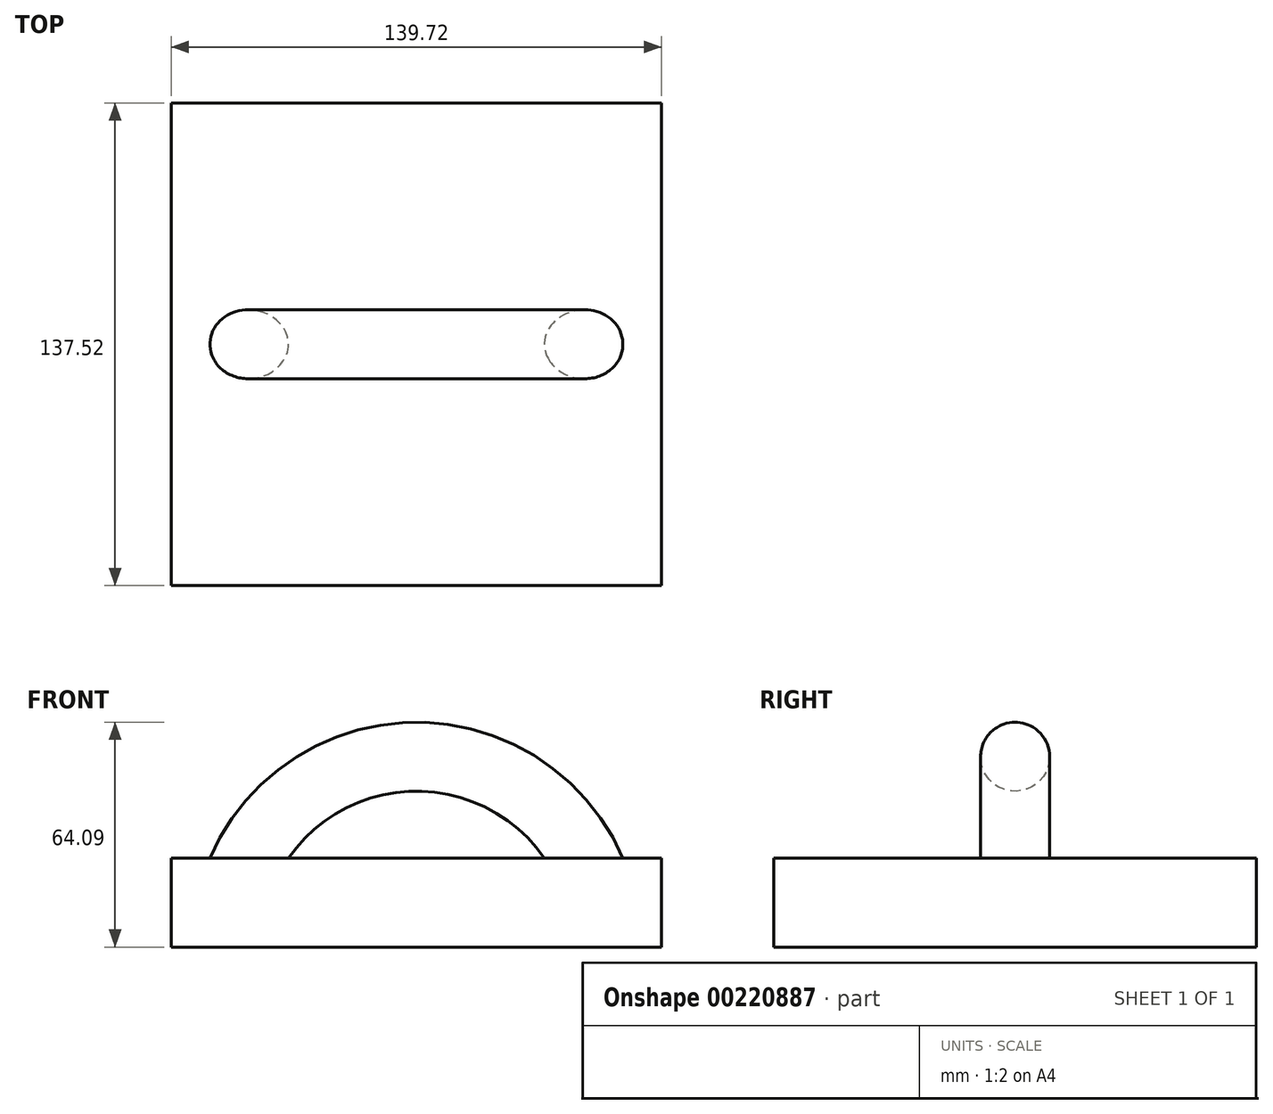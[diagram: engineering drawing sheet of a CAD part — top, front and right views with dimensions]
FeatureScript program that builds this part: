
annotation { "Feature Type Name" : "Feature", "Feature Type Description" : "" }
export const myFeature = defineFeature(function(context is Context, id is Id, definition is map)
    precondition{}
    {
        {
            var Q0;
            Q0=qCreatedBy(makeId("Top.planeOp"),FACE);
            var sketch = newSketch(context, id + "F0", { "sketchPlane" : qUnion([Q0])});
            skLineSegment(sketch, "E0.bottom", {"start": v(69.86, -68.76) * mm, "end": v(-69.86, -68.76) * mm});
            skLineSegment(sketch, "E0.top", {"start": v(69.86, 68.76) * mm, "end": v(-69.86, 68.76) * mm});
            skLineSegment(sketch, "E0.left", {"start": v(69.86, -68.76) * mm, "end": v(69.86, 68.76) * mm});
            skLineSegment(sketch, "E0.right", {"start": v(-69.86, -68.76) * mm, "end": v(-69.86, 68.76) * mm});
            skPoint(sketch, "E0.middle", {"position": v(0, 0) * mm});
            skLineSegment(sketch, "E1", {"start": v(0, 68.76) * mm, "end": v(0, -68.76) * mm});
            skSolve(sketch);
        }
        {
            var Q0;
            Q0=qCreatedBy(makeId("Top.planeOp"),FACE);
            var sketch = newSketch(context, id + "F1", { "sketchPlane" : qUnion([Q0])});
            skCircle(sketch, "E2", {"center": v(54.26, 0) * mm, "radius": 9.82 * mm});
            skSolve(sketch);
        }
        {
            var Q0;
            Q0=makeQuery(id+"F1.imprint","IMPRINT",FACE,{"disambiguationData":[TD([[makeQuery(id+"F1.imprint","IMPRINT",EDGE,{"derivedFrom":sQuery(id+"F1.wireOp",EDGE,"E2")}),1.0]])]});
            var Q1;
            Q1=sQuery(id+"F0.wireOp",EDGE,"E1");
            revolve(context, id + "F2", {"entities" : qUnion([Q0]), "axis" : qUnion([Q1]), "revolveType" : RevolveType.ONE_DIRECTION, "angle" : 180 * degree});
        }
        {
            var Q0;
            {var subQ0=sQuery(id+"F0.wireOp",EDGE,"E0.right");Q0=makeQuery(id+"F0.imprint","IMPRINT",FACE,{"disambiguationData":[TD([[makeQuery(id+"F0.imprint","IMPRINT",EDGE,{"derivedFrom":subQ0}),-1.0]])]});}
            var Q1;
            {var subQ0=sQuery(id+"F0.wireOp",EDGE,"E0.left");Q1=makeQuery(id+"F0.imprint","IMPRINT",FACE,{"disambiguationData":[TD([[makeQuery(id+"F0.imprint","IMPRINT",EDGE,{"derivedFrom":subQ0}),1.0]])]});}
            extrude(context, id + "F3", {"entities" : qUnion([Q0, Q1]), "operationType" : NewBodyOperationType.ADD, "depth" : 25.4 * mm});
        }
    });
